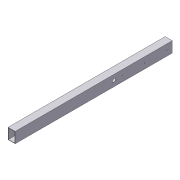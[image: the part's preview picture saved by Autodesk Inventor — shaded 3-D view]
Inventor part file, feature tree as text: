
AUTODESK INVENTOR PART (.ipt)
format: ipt  version: 2012 (Build 160160000, 160)  size: 93,184 bytes
history: native  units: in
note: dims shown in document units (in); Inventor stores cm internally (conversion verified against a paired STEP export)
features: hole x2, extrude x1, pattern_linear x1, sketch x1
ambient origin geometry x8: Origin, YZ Plane, XZ Plane, XY Plane, X Axis, Y Axis, Z Axis, Center Point
bodies: Solid1 (feature_tree)
feature tree (5):
  extrude  "Extrusion1"  Depth=0.125in
  hole  "Hole1"  [1 undecoded]
  hole  "Hole2"  [1 undecoded]
  pattern_linear  "Rectangular Pattern1"  Count1=3 Spacing1=6.25in
  sketch  "Sketch1"  dims[d4=44.0in d5=0.0in d13=0.125in d14=2.0in d15=3.0in d40=16.25in d41=1.5in d18=1.0in d19=0.75in d20=0.375in d21=0.25in d22=0.5635in d23=1.0in d24=0.8108in d42=1.5in d43=1.5in d27=0.188in d28=0.75in d29=0.375in d30=0.25in d31=0.5635in d32=1.0in d33=0.8108in d34=1.1811in d36=6.25in d37=0.125in d38=0.125in d39=0.125in]
note: 2 required parameter values undecoded (feature->parameter linkage not recoverable at this tier; creation-order binding heuristic only, values carry confidence <= 0.55)
